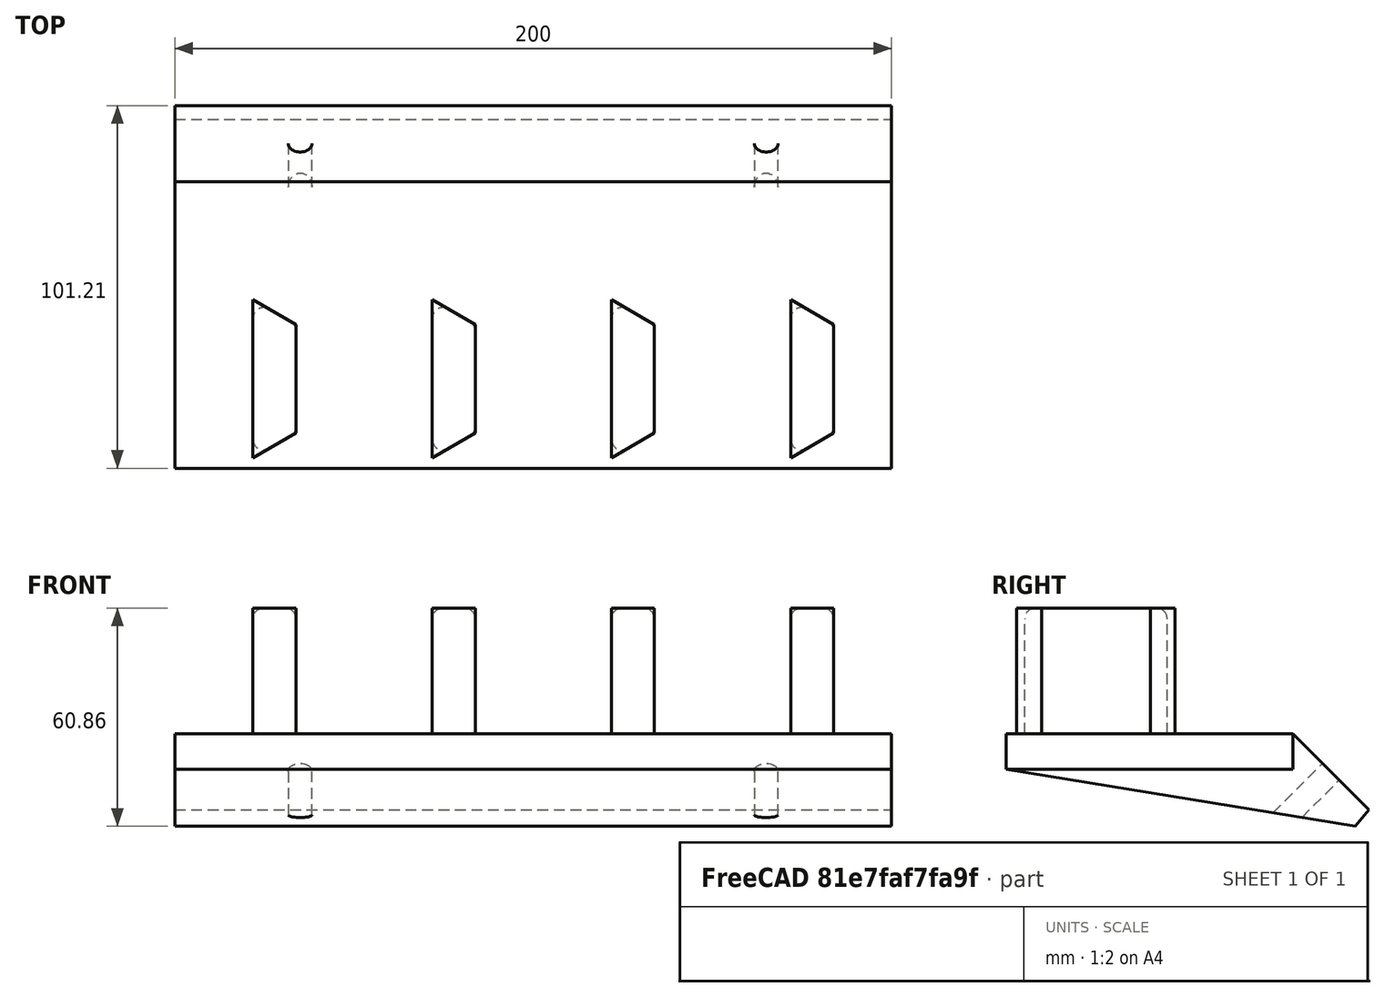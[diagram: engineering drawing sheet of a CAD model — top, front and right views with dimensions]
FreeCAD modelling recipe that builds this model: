
FCSTD DOCUMENT  (FreeCAD 0.16R)
Label: BXAholder
License: All rights reserved
LicenseURL: http://en.wikipedia.org/wiki/All_rights_reserved
objects: Sketcher::SketchObject×4, PartDesign::Pad×3, PartDesign::Fillet×2, PartDesign::LinearPattern×1, PartDesign::Pocket×1, Mesh::Feature×1
note: 15 computed .brp shape members not serialized (recipe doc carries the construction recipe); baked Part::Feature solids carry a one-line shape summary decoded from their .brp

FEATURE [Sketcher::SketchObject] Sketch001
  sketch-geometry (4):
    g0: LineSegment StartX=-25 StartY=55 StartZ=0 EndX=175 EndY=55 EndZ=0
    g1: LineSegment StartX=175 StartY=55 StartZ=0 EndX=175 EndY=-25 EndZ=0
    g2: LineSegment StartX=175 StartY=-25 StartZ=0 EndX=-25 EndY=-25 EndZ=0
    g3: LineSegment StartX=-25 StartY=-25 StartZ=0 EndX=-25 EndY=55 EndZ=0
  constraints (12):
    c: Coincident(g0,g1)
    c: Coincident(g1,g2)
    c: Coincident(g2,g3)
    c: Coincident(g3,g0)
    c: Horizontal(g0)
    c: Horizontal(g2)
    c: Vertical(g1)
    c: Vertical(g3)
    c: Distance(g2) = 200
    c: Distance(g1) = 80
    c: DistanceX(g-2,g0) = -25
    c: DistanceY(g0) = 55
FEATURE [PartDesign::Pad] Pad
  Length = 10
  Length2 = 100
  Reversed = true
  Sketch = -> Sketch001
  Type = 0
FEATURE [Sketcher::SketchObject] Sketch
  Support = -> Pad [Face5]
  sketch-geometry (8):
    g0: Circle [constr] CenterX=0 CenterY=16.575 CenterZ=0 NormalX=0 NormalY=0 NormalZ=1 Radius=3.175
    g1: Circle [constr] CenterX=0 CenterY=-16.575 CenterZ=0 NormalX=0 NormalY=0 NormalZ=1 Radius=3.175
    g2: LineSegment [constr] StartX=0 StartY=50 StartZ=0 EndX=0 EndY=-50 EndZ=0
    g3: Circle [constr] CenterX=0 CenterY=0 CenterZ=0 NormalX=0 NormalY=0 NormalZ=1 Radius=13.4
    g4: LineSegment StartX=-3.175 StartY=22.0743 StartZ=0 EndX=-3.175 EndY=-22.0743 EndZ=0
    g5: LineSegment StartX=-3.175 StartY=-22.0743 StartZ=0 EndX=8.825 EndY=-15.1461 EndZ=0
    g6: LineSegment StartX=8.825 StartY=-15.1461 StartZ=0 EndX=8.825 EndY=15.1461 EndZ=0
    g7: LineSegment StartX=8.825 StartY=15.1461 StartZ=0 EndX=-3.175 EndY=22.0743 EndZ=0
  constraints (25):
    c: Radius(g1) = 3.175
    c: Radius(g0) = 3.175
    c: Vertical(g2)
    c: PointOnObject(g1,g2)
    c: PointOnObject(g0,g2)
    c: Radius(g3) = 13.4
    c: PointOnObject(g3,g2)
    c: Tangent(g1,g3)
    c: Tangent(g3,g0)
    c: PointOnObject(g3,g-1)
    c: Vertical(g4)
    c: Coincident(g4,g5)
    c: Coincident(g5,g6)
    c: Vertical(g6)
    c: Coincident(g6,g7)
    c: Coincident(g7,g4)
    c: Tangent(g4,g0)
    c: Tangent(g5,g1)
    c: Tangent(g7,g0)
    c: Angle(g4,g7) = 1.0472
    c: Angle(g5,g4) = 1.0472
    c: Distance(g6,g4) = 12
    c: Coincident(g3,g-1)
    c: Distance(g2) = 100
    c: Symmetric(g2,g2,g-1)
FEATURE [PartDesign::Pad] Pad001
  Length = 35
  Length2 = 100
  Sketch = -> Sketch
  Type = 0
FEATURE [PartDesign::LinearPattern] LinearPattern
  Direction = -> Pad001 [Face2]
  Length = 150
  Occurrences = 4
  Originals = -> [Pad001]
FEATURE [Sketcher::SketchObject] Sketch002
  ExternalGeometry = -> [LinearPattern]
  Placement = pos=(-25,0,0) rot=(0.57735,-0.57735,-0.57735;2.0944rad)
  Support = -> LinearPattern [Face2]
  sketch-geometry (4):
    g0: LineSegment StartX=-55 StartY=0 StartZ=0 EndX=-76.2132 EndY=-21.2132 EndZ=0
    g1: LineSegment StartX=-76.2132 StartY=-21.2132 StartZ=0 EndX=-72.4172 EndY=-25.8598 EndZ=0
    g2: LineSegment StartX=-72.4172 StartY=-25.8598 StartZ=0 EndX=25 EndY=-10 EndZ=0
    g3: LineSegment StartX=-55 StartY=0 StartZ=0 EndX=25 EndY=-10 EndZ=0
  constraints (10):
    c: Coincident(g-5,g0)
    c: Coincident(g0,g1)
    c: Coincident(g1,g2)
    c: Angle(g0,g-1) = 2.35619
    c: Distance(g0) = 30
    c: Distance(g1) = 6
    c: Coincident(g3,g0)
    c: Coincident(g3,g2)
    c: Coincident(g2,g-4)
    c: Angle(g2,g1) = 2.0944
FEATURE [PartDesign::Pad] Pad002
  Length = 200
  Length2 = 100
  Reversed = true
  Sketch = -> Sketch002
  Type = 0
FEATURE [Sketcher::SketchObject] Sketch003
  ExternalGeometry = -> [Pad002]
  Placement = pos=(0,27.5,27.5) rot=(0,0.382683,0.92388;3.14159rad)
  Support = -> Pad002 [Face7]
  sketch-geometry (3):
    g0: Circle CenterX=-140 CenterY=-53.8909 CenterZ=0 NormalX=0 NormalY=0 NormalZ=1 Radius=3.3
    g1: Circle CenterX=-10 CenterY=-53.8909 CenterZ=0 NormalX=0 NormalY=0 NormalZ=1 Radius=3.3
    g2: LineSegment [constr] StartX=-175 StartY=-53.8909 StartZ=0 EndX=25 EndY=-53.8909 EndZ=0
  constraints (9):
    c: Horizontal(g2)
    c: Symmetric(g-3,g-3,g2)
    c: Symmetric(g-4,g-4,g2)
    c: PointOnObject(g0,g2)
    c: PointOnObject(g1,g2)
    c: Radius(g0) = 3.3
    c: Equal(g0,g1)
    c: Distance(g0,g2) = 35
    c: Distance(g1,g2) = 35
FEATURE [PartDesign::Pocket] Pocket
  Length = 5
  Sketch = -> Sketch003
  Type = 1
FEATURE [PartDesign::Fillet] Fillet
  Base = -> Pocket [Edge45,Edge5,Edge47,Edge55,Edge57,Edge49,Edge42,Edge1,Edge58,Edge61,Edge53,Edge50,Edge39,Edge41,Edge4,Edge28]
  Radius = 3
FEATURE [PartDesign::Fillet] Fillet001
  Base = -> Fillet [Edge87,Edge91,Edge83,Edge94,Edge81,Edge93,Edge85,Edge89,Edge103,Edge107,Edge99,Edge110,Edge97,Edge109,Edge101,Edge105,Edge73,Edge69,Edge77,Edge65,Edge78,Edge67,Edge75,Edge71,Edge44,Edge45,Edge46,Edge47,Edge48,Edge43,Edge41,Edge4]
  Radius = 3
FEATURE [Mesh::Feature] Mesh  label="Fillet001 (Meshed)"
